annotation { "Feature Type Name" : "Feature", "Feature Type Description" : "" }
export const myFeature = defineFeature(function(context is Context, id is Id, definition is map)
    precondition{}
    {
        {
            var Q0;
            Q0=qCreatedBy(makeId("Front.planeOp"),FACE);
            var sketch = newSketch(context, id + "F0", { "sketchPlane" : qUnion([Q0])});
            skLineSegment(sketch, "E0.bottom", {"start": v(-80.5, 48) * mm, "end": v(80.5, 48) * mm});
            skLineSegment(sketch, "E0.top", {"start": v(-80.5, -48) * mm, "end": v(80.5, -48) * mm});
            skLineSegment(sketch, "E0.left", {"start": v(-80.5, 48) * mm, "end": v(-80.5, -48) * mm});
            skLineSegment(sketch, "E0.right", {"start": v(80.5, 48) * mm, "end": v(80.5, -48) * mm});
            skPoint(sketch, "E0.middle", {"position": v(0, 0) * mm});
            skLineSegment(sketch, "E1.bottom", {"start": v(-64, 38) * mm, "end": v(64, 38) * mm});
            skLineSegment(sketch, "E1.top", {"start": v(-64, -38) * mm, "end": v(64, -38) * mm});
            skLineSegment(sketch, "E1.left", {"start": v(-64, 38) * mm, "end": v(-64, -38) * mm});
            skLineSegment(sketch, "E1.right", {"start": v(64, 38) * mm, "end": v(64, -38) * mm});
            skSolve(sketch);
        }
        {
            var Q0;
            Q0 = qSketchRegion(id + "F0", true);
            extrude(context, id + "F1", {"entities" : qUnion([Q0]), "depth" : 1 * mm});
        }
        {
            var Q0;
            Q0=qCreatedBy(makeId("Front.planeOp"),FACE);
            var sketch = newSketch(context, id + "F2", { "sketchPlane" : qUnion([Q0])});
            skLineSegment(sketch, "E2.0.0", {"start": v(80.5, 48) * mm, "end": v(-80.5, 48) * mm});
            skLineSegment(sketch, "E2.0.1", {"start": v(-80.5, 48) * mm, "end": v(-80.5, -48) * mm});
            skLineSegment(sketch, "E2.0.2", {"start": v(-80.5, -48) * mm, "end": v(80.5, -48) * mm});
            skLineSegment(sketch, "E2.0.3", {"start": v(80.5, -48) * mm, "end": v(80.5, 48) * mm});
            skPoint(sketch, "E3.endSnap0", {"position": v(0, 48) * mm});
            skLineSegment(sketch, "E4.0", {"start": v(-64, 38) * mm, "end": v(64, 38) * mm});
            skLineSegment(sketch, "E5.0", {"start": v(-64, -38) * mm, "end": v(64, -38) * mm});
            skLineSegment(sketch, "E6.bottom", {"start": v(-31.5, 38) * mm, "end": v(31.5, 38) * mm});
            skLineSegment(sketch, "E6.top", {"start": v(-31.5, -38) * mm, "end": v(31.5, -38) * mm});
            skLineSegment(sketch, "E6.left", {"start": v(-31.5, 38) * mm, "end": v(-31.5, -38) * mm});
            skLineSegment(sketch, "E6.right", {"start": v(31.5, 38) * mm, "end": v(31.5, -38) * mm});
            skPoint(sketch, "E6.middle", {"position": v(0, 0) * mm});
            skLineSegment(sketch, "E7.bottom", {"start": v(31.5, 38) * mm, "end": v(32.5, 38) * mm});
            skLineSegment(sketch, "E7.top", {"start": v(31.5, -38) * mm, "end": v(32.5, -38) * mm});
            skLineSegment(sketch, "E7.right", {"start": v(32.5, 38) * mm, "end": v(32.5, -38) * mm});
            skLineSegment(sketch, "E8.bottom", {"start": v(-64, -38) * mm, "end": v(-32.5, -38) * mm});
            skLineSegment(sketch, "E8.top", {"start": v(-64, 38) * mm, "end": v(-32.5, 38) * mm});
            skLineSegment(sketch, "E8.left", {"start": v(-64, -38) * mm, "end": v(-64, 38) * mm});
            skLineSegment(sketch, "E8.right", {"start": v(-32.5, -38) * mm, "end": v(-32.5, 38) * mm});
            skSolve(sketch);
        }
        {
            var Q0;
            Q0=makeQuery(id+"F2.imprint","IMPRINT",FACE,{"disambiguationData":[TD([[makeQuery(id+"F2.imprint","IMPRINT",EDGE,{"derivedFrom":sQuery(id+"F2.wireOp",EDGE,"E8.bottom")}),1.0]])]});
            var Q1;
            Q1=makeQuery(id+"F2.imprint","IMPRINT",FACE,{"disambiguationData":[TD([[makeQuery(id+"F2.imprint","IMPRINT",EDGE,{"derivedFrom":sQuery(id+"F2.wireOp",EDGE,"E6.bottom")}),-1.0]])]});
            var Q2;
            Q2=makeQuery(id+"F2.imprint","IMPRINT",FACE,{"disambiguationData":[TD([[makeQuery(id+"F2.imprint","IMPRINT",EDGE,{"derivedFrom":sQuery(id+"F2.wireOp",EDGE,"E2.0.0")}),1.0]])]});
            extrude(context, id + "F3", {"entities" : qUnion([Q0, Q1, Q2]), "operationType" : NewBodyOperationType.ADD, "depth" : 0.5 * mm});
        }
        {
            var Q0;
            {var subQ0=sQuery(id+"F2.wireOp",EDGE,"E8.right");Q0=makeQuery(id+"F3.boolean.opBoolean","SPLIT",FACE,{"disambiguationData":[TD([makeQuery(id+"F1.opExtrude","SWEPT_FACE",FACE,{"disambiguationData":[OSD([sQuery(id+"F0.wireOp",EDGE,"E1.left")])]})])],"derivedFrom":makeQuery(id+"F3.opExtrude","CAP_FACE",FACE,{"disambiguationData":[OSD([sQuery(id+"F2.wireOp",EDGE,"E2.0.0"),sQuery(id+"F2.wireOp",EDGE,"E2.0.1"),sQuery(id+"F2.wireOp",EDGE,"E2.0.2"),sQuery(id+"F2.wireOp",EDGE,"E2.0.3"),sQuery(id+"F2.wireOp",EDGE,"E4.0"),sQuery(id+"F2.wireOp",EDGE,"E5.0"),sQuery(id+"F2.wireOp",EDGE,"E6.left"),sQuery(id+"F2.wireOp",EDGE,"E7.bottom"),sQuery(id+"F2.wireOp",EDGE,"E7.top"),sQuery(id+"F2.wireOp",EDGE,"E6.right"),sQuery(id+"F2.wireOp",EDGE,"E7.right"),subQ0])],"isStart":false})});}
            var sketch = newSketch(context, id + "F4", { "sketchPlane" : qUnion([Q0])});
            skText(sketch, "E9", { "text": "Overlap Finseal\n\n", "fontName": "AllertaStencil-Regular.ttf"});
            skText(sketch, "E10", { "text": "Front text", "fontName": "AllertaStencil-Regular.ttf"});
            skPoint(sketch, "E11", {"position": v(0, 23.78) * mm});
            skText(sketch, "E12", { "text": "Back tekst", "fontName": "AllertaStencil-Regular.ttf"});
            skText(sketch, "E13", { "text": "Back text", "fontName": "AllertaStencil-Regular.ttf"});
            skLineSegment(sketch, "E14", {"start": v(-48.25, 38) * mm, "end": v(-48.25, -38) * mm, "construction": true});
            skLineSegment(sketch, "E15", {"start": v(-48.25, 38) * mm, "end": v(-32.5, 38) * mm, "construction": true});
            skLineSegment(sketch, "E16", {"start": v(-40.38, 38) * mm, "end": v(-40.38, -38) * mm, "construction": true});
            skLineSegment(sketch, "E17", {"start": v(-40.38, 17.75) * mm, "end": v(-40.38, -17.75) * mm, "construction": true});
            skLineSegment(sketch, "E18", {"start": v(0, 17.75) * mm, "end": v(0, -17.75) * mm, "construction": true});
            skLineSegment(sketch, "E19", {"start": v(-64, 38) * mm, "end": v(-48.25, 38) * mm, "construction": true});
            skLineSegment(sketch, "E20", {"start": v(-56.12, 38) * mm, "end": v(-56.12, -38) * mm, "construction": true});
            skLineSegment(sketch, "E21", {"start": v(-56.12, 17.75) * mm, "end": v(-56.12, -17.75) * mm, "construction": true});
            skLineSegment(sketch, "E22.0.0", {"start": v(64, 38) * mm, "end": v(32.5, 38) * mm});
            skLineSegment(sketch, "E22.0.1", {"start": v(32.5, 38) * mm, "end": v(32.5, -38) * mm});
            skLineSegment(sketch, "E22.0.2", {"start": v(32.5, -38) * mm, "end": v(64, -38) * mm});
            skLineSegment(sketch, "E22.0.3", {"start": v(64, -38) * mm, "end": v(64, 38) * mm});
            skLineSegment(sketch, "E23", {"start": v(32.5, 38) * mm, "end": v(64, 38) * mm, "construction": true});
            skLineSegment(sketch, "E24", {"start": v(48.25, 38) * mm, "end": v(48.25, -38) * mm, "construction": true});
            skLineSegment(sketch, "E25", {"start": v(48.25, 17.75) * mm, "end": v(48.25, -17.75) * mm, "construction": true});
            const initialGuessF4  = {"E9": [-0.07266, -0.03, 0, 1, 0.00544], "E10": [0.00424, -0.03, 0, 1, 0.00848], "E12": [0.06888, -0.03, 0, 1, 0.00826], "E13": [-0.04962, -0.03, 0, 1, 0.009]};
            skSetInitialGuess(sketch, initialGuessF4);
            skSolve(sketch);
        }
        {
            var Q0;
            Q0 = qSketchRegion(id + "F4", true);
            extrude(context, id + "F5", {"entities" : qUnion([Q0]), "operationType" : NewBodyOperationType.ADD, "depth" : 0.3 * mm});
        }
        {
            var Q0;
            Q0=makeQuery(id+"F1.opExtrude","CAP_FACE",FACE,{"disambiguationData":[OSD([sQuery(id+"F0.wireOp",EDGE,"E0.bottom"),sQuery(id+"F0.wireOp",EDGE,"E0.top"),sQuery(id+"F0.wireOp",EDGE,"E0.left"),sQuery(id+"F0.wireOp",EDGE,"E0.right"),sQuery(id+"F0.wireOp",EDGE,"E1.bottom"),sQuery(id+"F0.wireOp",EDGE,"E1.top"),sQuery(id+"F0.wireOp",EDGE,"E1.left"),sQuery(id+"F0.wireOp",EDGE,"E1.right")])],"isStart":false});
            var sketch = newSketch(context, id + "F6", { "sketchPlane" : qUnion([Q0])});
            skLineSegment(sketch, "E26.bottom", {"start": v(-80.5, 3) * mm, "end": v(-68.5, 3) * mm});
            skLineSegment(sketch, "E26.top", {"start": v(-80.5, -3) * mm, "end": v(-68.5, -3) * mm});
            skLineSegment(sketch, "E26.left", {"start": v(-80.5, 3) * mm, "end": v(-80.5, -3) * mm});
            skLineSegment(sketch, "E26.right", {"start": v(-68.5, 3) * mm, "end": v(-68.5, -3) * mm});
            skPoint(sketch, "E27", {"position": v(-68.5, 0) * mm});
            skPoint(sketch, "E28", {"position": v(-80.5, 0) * mm});
            skSolve(sketch);
        }
        {
            var Q0;
            Q0=makeQuery(id+"F6.imprint","IMPRINT",FACE,{"disambiguationData":[TD([[makeQuery(id+"F6.imprint","IMPRINT",EDGE,{"derivedFrom":sQuery(id+"F6.wireOp",EDGE,"E26.bottom")}),-1.0]])]});
            extrude(context, id + "F7", {"entities" : qUnion([Q0]), "operationType" : NewBodyOperationType.ADD, "depth" : 1 * mm});
        }
    });